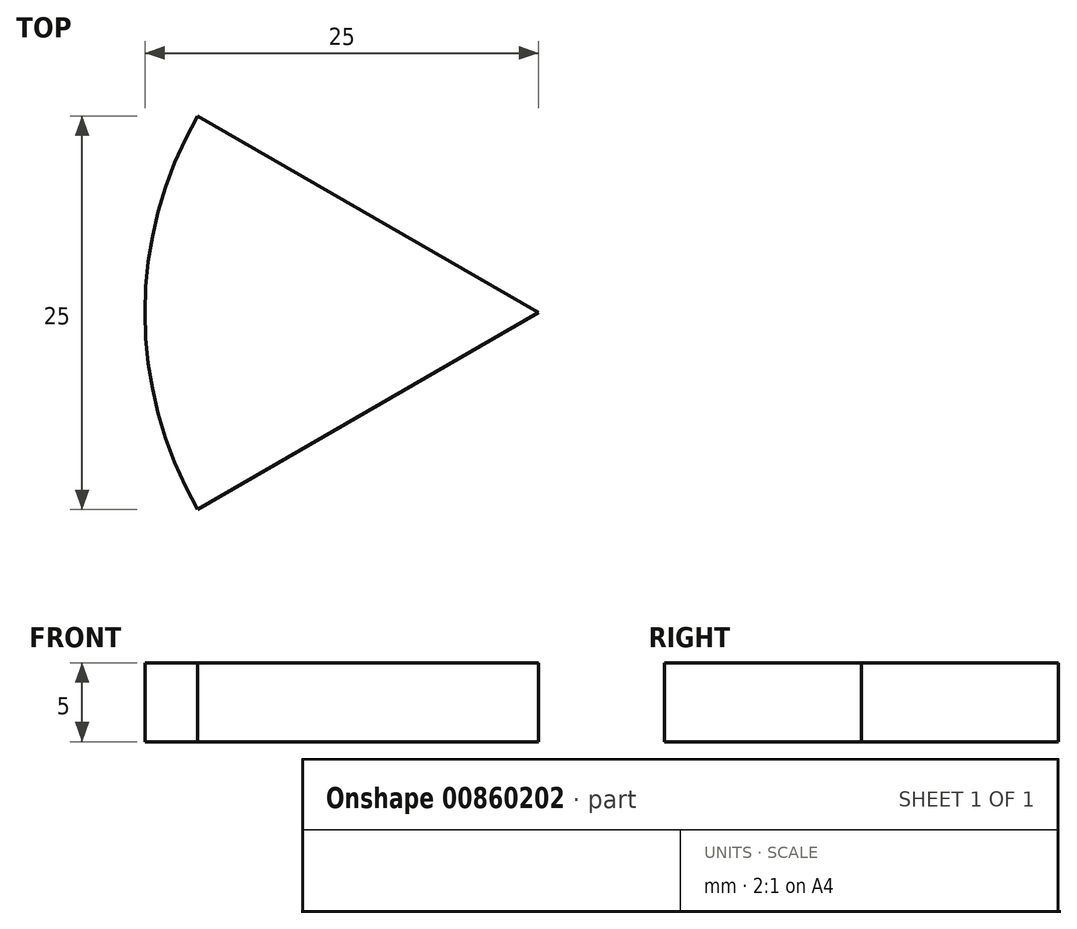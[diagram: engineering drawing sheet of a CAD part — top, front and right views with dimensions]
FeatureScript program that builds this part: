
annotation { "Feature Type Name" : "Feature", "Feature Type Description" : "" }
export const myFeature = defineFeature(function(context is Context, id is Id, definition is map)
    precondition{}
    {
        {
            var Q0;
            Q0=qCreatedBy(makeId("Front.planeOp"),FACE);
            var sketch = newSketch(context, id + "F0", { "sketchPlane" : qUnion([Q0])});
            skLineSegment(sketch, "E0.bottom", {"start": v(0, 0) * mm, "end": v(25, 0) * mm});
            skLineSegment(sketch, "E0.top", {"start": v(0, -5) * mm, "end": v(25, -5) * mm});
            skLineSegment(sketch, "E0.left", {"start": v(0, 0) * mm, "end": v(0, -5) * mm});
            skLineSegment(sketch, "E0.right", {"start": v(25, 0) * mm, "end": v(25, -5) * mm});
            skSolve(sketch);
        }
        {
            var Q0;
            Q0=makeQuery(id+"F0.imprint","IMPRINT",FACE,{"disambiguationData":[TD([[makeQuery(id+"F0.imprint","IMPRINT",EDGE,{"derivedFrom":sQuery(id+"F0.wireOp",EDGE,"E0.bottom")}),-1.0]])]});
            var Q1;
            Q1=sQuery(id+"F0.wireOp",EDGE,"E0.right");
            revolve(context, id + "F1", {"surfaceOperationType" : NewSurfaceOperationType.NEW, "entities" : qUnion([Q0]), "axis" : qUnion([Q1]), "revolveType" : RevolveType.TWO_DIRECTIONS, "angle" : 30 * degree, "angleBack" : 330 * degree});
        }
    });
